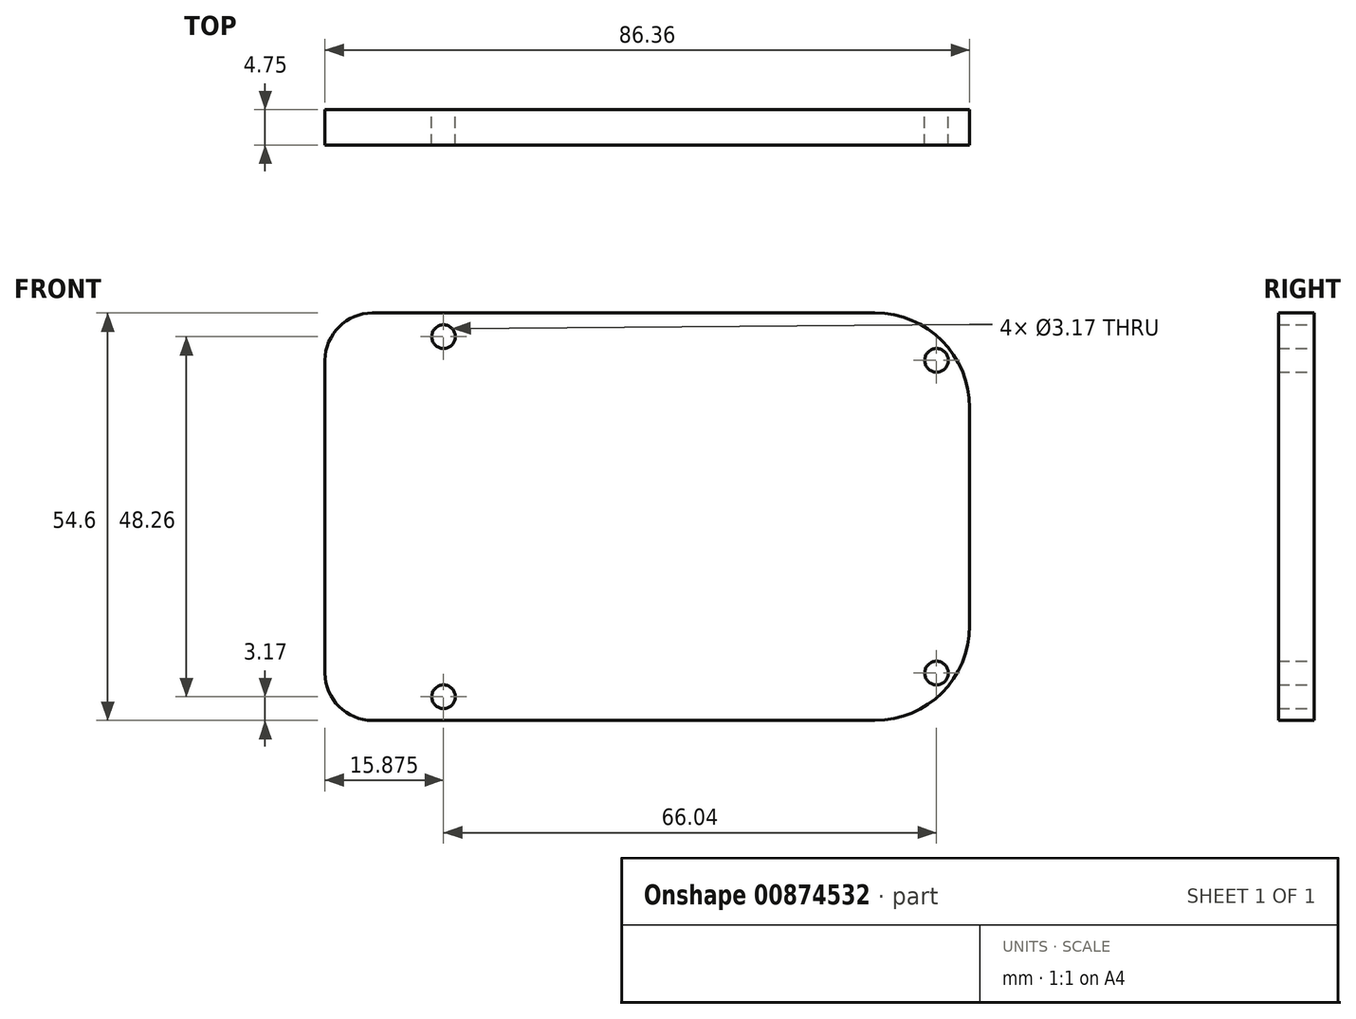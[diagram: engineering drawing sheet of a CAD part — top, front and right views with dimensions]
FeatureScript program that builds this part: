
annotation { "Feature Type Name" : "Feature", "Feature Type Description" : "" }
export const myFeature = defineFeature(function(context is Context, id is Id, definition is map)
    precondition{}
    {
        {
            var Q0;
            Q0=qCreatedBy(makeId("Front.planeOp"),FACE);
            var sketch = newSketch(context, id + "F0", { "sketchPlane" : qUnion([Q0])});
            skLineSegment(sketch, "E0.bottom", {"start": v(30.48, 27.3) * mm, "end": v(-36.83, 27.3) * mm});
            skLineSegment(sketch, "E0.top", {"start": v(30.48, -27.3) * mm, "end": v(-36.83, -27.3) * mm});
            skLineSegment(sketch, "E0.left", {"start": v(43.18, 14.6) * mm, "end": v(43.18, -14.6) * mm});
            skLineSegment(sketch, "E0.right", {"start": v(-43.18, 20.95) * mm, "end": v(-43.18, -20.96) * mm});
            skPoint(sketch, "E0.middle", {"position": v(0, 0) * mm});
            skCircle(sketch, "E1", {"center": v(-27.3, 24.13) * mm, "radius": 1.59 * mm});
            skCircle(sketch, "E2", {"center": v(-27.3, -24.13) * mm, "radius": 1.59 * mm});
            skCircle(sketch, "E3", {"center": v(38.74, 20.96) * mm, "radius": 1.59 * mm});
            skCircle(sketch, "E4", {"center": v(38.74, -20.96) * mm, "radius": 1.59 * mm});
            skPoint(sketch, "E5.visualSharp", {"position": v(-43.18, 27.3) * mm});
            skArc(sketch, "E5.filletArc", {"start": v(-36.83, 27.3) * mm, "mid": v(-41.32, 25.45) * mm, "end": v(-43.18, 20.95) * mm});
            skPoint(sketch, "E6.visualSharp", {"position": v(-43.18, -27.3) * mm});
            skArc(sketch, "E6.filletArc", {"start": v(-43.18, -20.96) * mm, "mid": v(-41.32, -25.45) * mm, "end": v(-36.83, -27.3) * mm});
            skPoint(sketch, "E7.visualSharp", {"position": v(43.18, 27.3) * mm});
            skArc(sketch, "E7.filletArc", {"start": v(43.18, 14.6) * mm, "mid": v(39.46, 23.59) * mm, "end": v(30.48, 27.3) * mm});
            skPoint(sketch, "E8.visualSharp", {"position": v(43.18, -27.3) * mm});
            skArc(sketch, "E8.filletArc", {"start": v(30.48, -27.3) * mm, "mid": v(39.46, -23.59) * mm, "end": v(43.18, -14.6) * mm});
            skSolve(sketch);
        }
        {
            var Q0;
            Q0=qSketchRegion(id+"F0",true);
            extrude(context, id + "F1", {"entities" : qUnion([Q0]), "depth" : 4.75 * mm, "offsetDistance" : 25.4 * mm});
        }
    });
